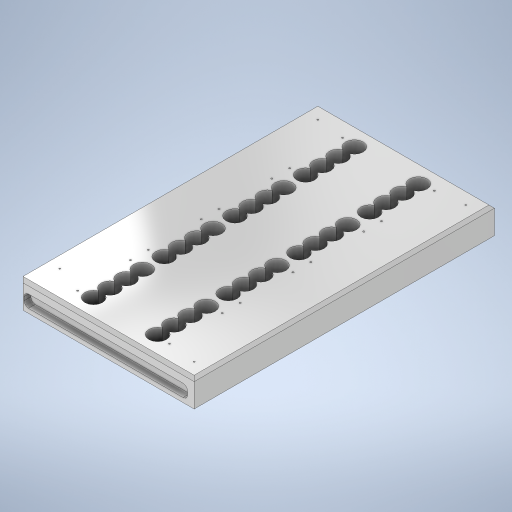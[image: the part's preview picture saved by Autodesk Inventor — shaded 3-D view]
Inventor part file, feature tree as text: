
AUTODESK INVENTOR PART (.ipt)
format: ipt  version: 2023 (Build 270158000, 158)  size: 522,240 bytes
history: native  units: in
note: dims shown in document units (in); Inventor stores cm internally (conversion verified against a paired STEP export)
features: sketch x6, extrude x4, hole x4, chamfer x2
ambient origin geometry x8: Origin, YZ Plane, XZ Plane, XY Plane, X Axis, Y Axis, Z Axis, Center Point
bodies: Solid1 (feature_tree)
feature tree (16):
  extrude  "Extrusion1"  Depth=8.5in
  hole  "Hole3"  [1 undecoded]
  hole  "Hole4"  [1 undecoded]
  extrude  "Extrusion4"  Depth=0.4075in
  extrude  "Extrusion5"  Depth=0.4075in
  hole  "Hole5"  [1 undecoded]
  chamfer  "Chamfer3"  Distance=2.0276in
  extrude  "Extrusion6"  Depth=5.0in
  hole  "Hole6"  [1 undecoded]
  chamfer  "Chamfer4"  Distance=0.3937in
  sketch  "Sketch1"  dims[d0=5.0in d1=8.5in]
  sketch  "Sketch5"  dims[d2=0.75in d3=0.0in d31=0.7894in]
  sketch  "Sketch6"  dims[d32=0.4075in d33=0.4075in]
  sketch  "Sketch8"  dims[d34=0.4075in d35=0.4075in]
  sketch  "Sketch11"  dims[d38=0.4075in d39=0.0402in d40=0.094in d41=0.119in d42=0.0787in d43=0.5635in d44=0.315in d45=0.8108in d46=1.4213in d47=2.0276in d48=0.5394in d49=1.4862in d50=1.5748in d52=2.0in d53=0.3937in d55=0.3937in d57=0.0465in d58=0.12in d59=0.1575in d60=0.0787in d61=90.0deg d62=0.315in d63=0.8108in d77=0.35in d78=0.1875in d79=0.1875in d80=0.125in d81=0.1875in d82=0.0in d83=0.125in d84=0.35in d88=0.125in d89=0.125in d91=0.1875in d92=0.0in d93=0.1875in d94=0.1875in d96=0.561in d97=0.4593in d99=0.156in d100=0.38in d101=0.5in d102=0.61in d103=0.5635in d104=1.0in d105=0.8108in d113=0.0787in d114=0.0787in d115=45.0deg d116=0.6299in d117=0.7087in d118=0.7087in d119=0.3543in d120=0.3543in d121=0.3543in d122=0.3543in d123=0.6299in d124=0.0787in d125=0.5in d126=0.0in d127=0.4593in d128=0.4593in d129=1.811in d130=1.378in d131=0.689in d132=0.9055in d133=1.2992in d134=0.748in d135=1.4961in d136=1.2992in d137=0.0465in d138=0.12in d139=0.119in d140=0.0787in d141=0.5635in d142=0.315in d143=0.8108in d144=1.5748in d146=2.0in d147=0.3937in d149=0.3937in d151=0.1575in d152=0.0787in d153=45.0deg d154=2.5in d155=5.0in d156=0.0148in d157=0.5635in d158=0.0295in d159=0.8108in d160=0.0025in d161=0.0295in d162=0.0148in]
  sketch  "Sketch9"  dims[d36=0.4075in d37=0.4075in]
note: 4 required parameter values undecoded (feature->parameter linkage not recoverable at this tier; creation-order binding heuristic only, values carry confidence <= 0.55)
